AUTODESK INVENTOR PART (.ipt)
format: ipt  version: 2016 (Build 200138000, 138)  size: 160,256 bytes
history: native  units: mm
features: sheet_metal_op x7, sketch x5, other x3, hole x2
ambient origin geometry x8: Origin, YZ Plane, XZ Plane, XY Plane, X Axis, Y Axis, Z Axis, Center Point
bodies: Solid1 (feature_tree)
feature tree (17):
  sheet_metal_op  "Face1"
  sheet_metal_op  "Flange1"
  sheet_metal_op  "Flange2"
  hole  "Hole1"  [1 undecoded]
  hole  "Hole2"  [1 undecoded]
  sketch  "Sketch1"  dims[d0=150.0mm d1=1695.0mm]
  other  "Plate1"
  sketch  "Sketch2"  dims[d2=1.6mm d3=1.6mm]
  other  "Plate2"
  sheet_metal_op  "Bend1"
  sheet_metal_op  "Corner1"
  sketch  "Sketch3"  dims[d4=0.8mm]
  other  "Plate3"
  sheet_metal_op  "Bend2"
  sheet_metal_op  "Corner2"
  sketch  "Sketch4"  dims[d5=3.2mm]
  sketch  "Sketch5"  dims[d6=1.6mm d7=380.0mm d8=6.981317mm d9=1.6mm d10=6.4mm d11=1.6mm d12=1.6mm d13=1.6mm d14=0.8mm d15=3.2mm d16=1.6mm d17=65.0mm d18=8.726646mm d19=1.6mm d20=6.4mm d21=1.6mm d22=1.6mm d24=12.0mm d26=25.0mm d27=15.0mm d28=12.0mm d29=15.0mm d30=12.0mm d31=12.0mm d32=25.0mm d33=25.0mm d34=12.0mm d35=6.0mm d36=4.0mm d37=2.0mm d38=90.0deg d39=1.6mm d40=20.594885mm d42=12.0mm d43=25.0mm d44=20.0mm d45=12.0mm d46=20.0mm d47=12.0mm d48=6.0mm d49=4.0mm d50=2.0mm d51=90.0deg d52=1.6mm d53=20.594885mm]
note: 2 required parameter values undecoded (feature->parameter linkage not recoverable at this tier; creation-order binding heuristic only, values carry confidence <= 0.55)
